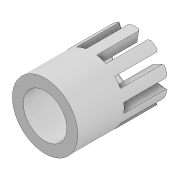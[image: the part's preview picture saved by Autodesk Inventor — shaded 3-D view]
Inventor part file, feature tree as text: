
AUTODESK INVENTOR PART (.ipt)
format: ipt  version: 2020 (Build 240168000, 168)  size: 203,776 bytes
history: native  units: in
note: dims shown in document units (in); Inventor stores cm internally (conversion verified against a paired STEP export)
features: extrude x2, sketch x2, chamfer x1, projected_geometry x1
ambient origin geometry x8: Origin, YZ Plane, XZ Plane, XY Plane, X Axis, Y Axis, Z Axis, Center Point
bodies: Solid1 (feature_tree)
feature tree (6):
  extrude  "Extrusion1"  Depth=0.315in
  extrude  "Extrusion2"  Depth=0.0787in
  chamfer  "Chamfer1"  Distance=0.0394in
  sketch  "Sketch1"  dims[d0=0.4724in d1=0.315in]
  sketch  "Sketch2"  dims[d2=0.3346in d3=0.0in d4=0.0787in d5=0.0394in d6=3.937in d8=360.0deg d10=0.315in d11=0.0in d12=0.0118in d13=0.125in d14=45.0deg]
  projected_geometry  "Projected Loop1"
